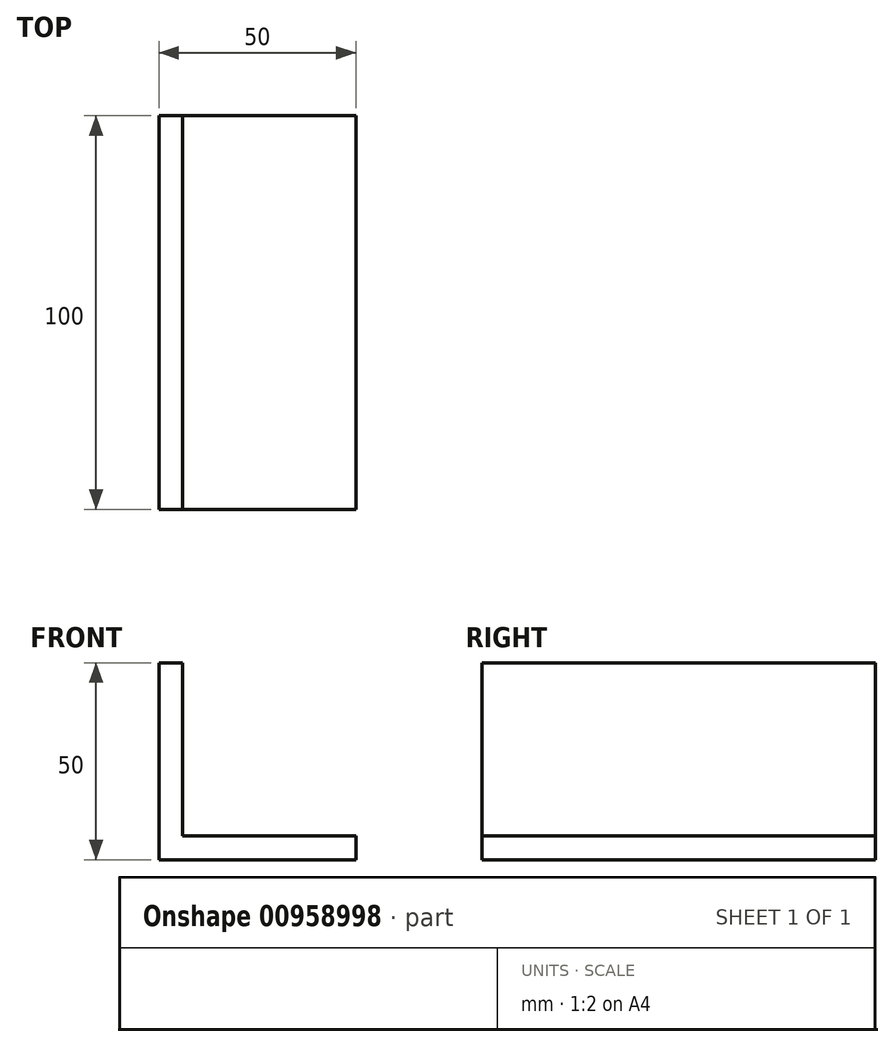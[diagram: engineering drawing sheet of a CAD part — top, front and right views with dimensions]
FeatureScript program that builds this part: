
annotation { "Feature Type Name" : "Feature", "Feature Type Description" : "" }
export const myFeature = defineFeature(function(context is Context, id is Id, definition is map)
    precondition{}
    {
        {
            var Q0;
            Q0=qCreatedBy(makeId("Front.planeOp"),FACE);
            var sketch = newSketch(context, id + "F0", { "sketchPlane" : qUnion([Q0])});
            skLineSegment(sketch, "E0", {"start": v(0, 0) * mm, "end": v(0, 50) * mm});
            skLineSegment(sketch, "E1", {"start": v(0, 50) * mm, "end": v(6, 50) * mm});
            skLineSegment(sketch, "E2", {"start": v(6, 50) * mm, "end": v(6, 6) * mm});
            skLineSegment(sketch, "E3", {"start": v(6, 6) * mm, "end": v(50, 6) * mm});
            skLineSegment(sketch, "E4", {"start": v(50, 6) * mm, "end": v(50, 0) * mm});
            skLineSegment(sketch, "E5", {"start": v(50, 0) * mm, "end": v(0, 0) * mm});
            skSolve(sketch);
        }
        {
            var Q0;
            Q0=qSketchRegion(id+"F0",true);
            extrude(context, id + "F1", {"entities" : qUnion([Q0]), "depth" : 100 * mm, "offsetDistance" : 25 * mm});
        }
    });
